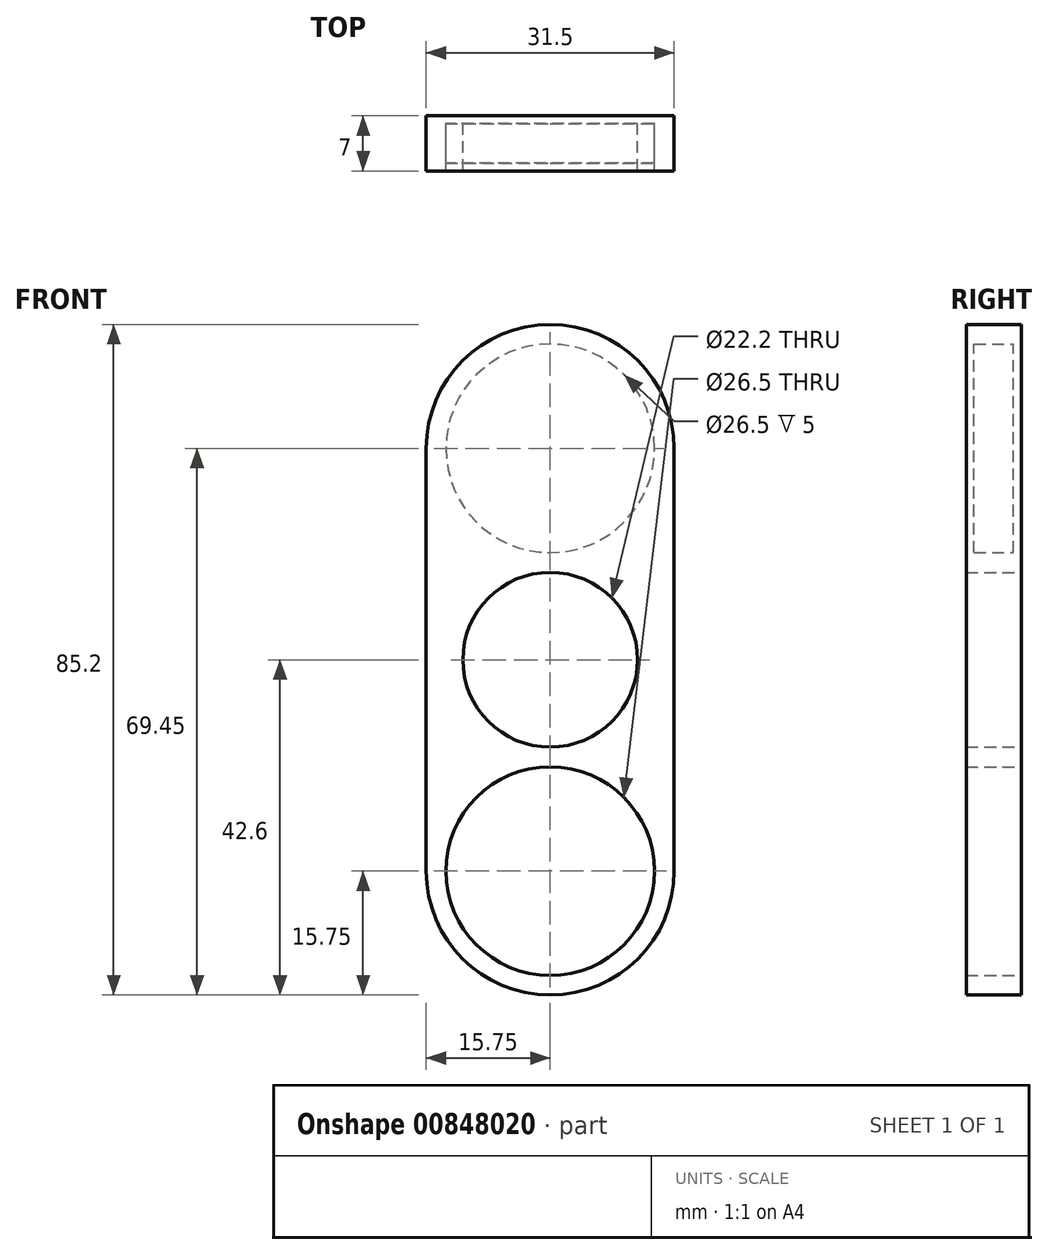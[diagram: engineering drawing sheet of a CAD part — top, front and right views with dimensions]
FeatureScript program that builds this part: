
annotation { "Feature Type Name" : "Feature", "Feature Type Description" : "" }
export const myFeature = defineFeature(function(context is Context, id is Id, definition is map)
    precondition{}
    {
        {
            var Q0;
            Q0=qCreatedBy(makeId("Front.planeOp"),FACE);
            var sketch = newSketch(context, id + "F0", { "sketchPlane" : qUnion([Q0])});
            skCircle(sketch, "E0", {"center": v(0, 0) * mm, "radius": 11.1 * mm});
            skCircle(sketch, "E1", {"center": v(0, 26.85) * mm, "radius": 13.25 * mm});
            skLineSegment(sketch, "E2", {"start": v(-31.9, 0) * mm, "end": v(39.55, 0) * mm, "construction": true});
            skArc(sketch, "E3", {"start": v(15.75, 26.85) * mm, "mid": v(0, 42.6) * mm, "end": v(-15.75, 26.85) * mm});
            skLineSegment(sketch, "E4", {"start": v(-15.75, 26.85) * mm, "end": v(-15.75, -26.85) * mm});
            skLineSegment(sketch, "E5", {"start": v(15.75, 26.85) * mm, "end": v(15.75, -26.85) * mm});
            skCircle(sketch, "E6.MirrorC", {"center": v(0, -26.85) * mm, "radius": 13.25 * mm});
            skArc(sketch, "E7.trimOffspring", {"start": v(15.75, -26.85) * mm, "mid": v(0, -42.6) * mm, "end": v(-15.75, -26.85) * mm});
            skSolve(sketch);
        }
        {
            var Q0;
            Q0=makeQuery(id+"F0.imprint","IMPRINT",FACE,{"disambiguationData":[TD([[makeQuery(id+"F0.imprint","IMPRINT",EDGE,{"derivedFrom":sQuery(id+"F0.wireOp",EDGE,"E0")}),-1.0]])]});
            extrude(context, id + "F1", {"entities" : qUnion([Q0]), "endBound" : BoundingType.SYMMETRIC, "depth" : 7 * mm, "offsetDistance" : 25 * mm});
        }
        {
            var Q0;
            Q0=makeQuery(id+"F0.imprint","IMPRINT",FACE,{"disambiguationData":[TD([[makeQuery(id+"F0.imprint","IMPRINT",EDGE,{"derivedFrom":sQuery(id+"F0.wireOp",EDGE,"E1")}),1.0]])]});
            var Q1;
            Q1=makeQuery(id+"F0.imprint","IMPRINT",FACE,{"disambiguationData":[TD([[makeQuery(id+"F0.imprint","IMPRINT",EDGE,{"derivedFrom":sQuery(id+"F0.wireOp",EDGE,"E6.MirrorC")}),-1.0]])]});
            extrude(context, id + "F2", {"entities" : qUnion([Q0, Q1]), "operationType" : NewBodyOperationType.ADD, "depth" : 3.5 * mm, "offsetDistance" : 25 * mm, "hasSecondDirection" : true, "secondDirectionOppositeDirection" : false, "secondDirectionDepth" : 2.5 * mm});
        }
        {
            var Q0;
            Q0=makeQuery(id+"F0.imprint","IMPRINT",FACE,{"disambiguationData":[TD([[makeQuery(id+"F0.imprint","IMPRINT",EDGE,{"derivedFrom":sQuery(id+"F0.wireOp",EDGE,"E1")}),1.0]])]});
            var Q1;
            Q1=makeQuery(id+"F0.imprint","IMPRINT",FACE,{"disambiguationData":[TD([[makeQuery(id+"F0.imprint","IMPRINT",EDGE,{"derivedFrom":sQuery(id+"F0.wireOp",EDGE,"E6.MirrorC")}),-1.0]])]});
            extrude(context, id + "F3", {"entities" : qUnion([Q0, Q1]), "operationType" : NewBodyOperationType.ADD, "oppositeDirection" : true, "depth" : 3.5 * mm, "offsetDistance" : 25 * mm, "hasSecondDirection" : true, "secondDirectionOppositeDirection" : true, "secondDirectionDepth" : 2.5 * mm});
        }
    });
